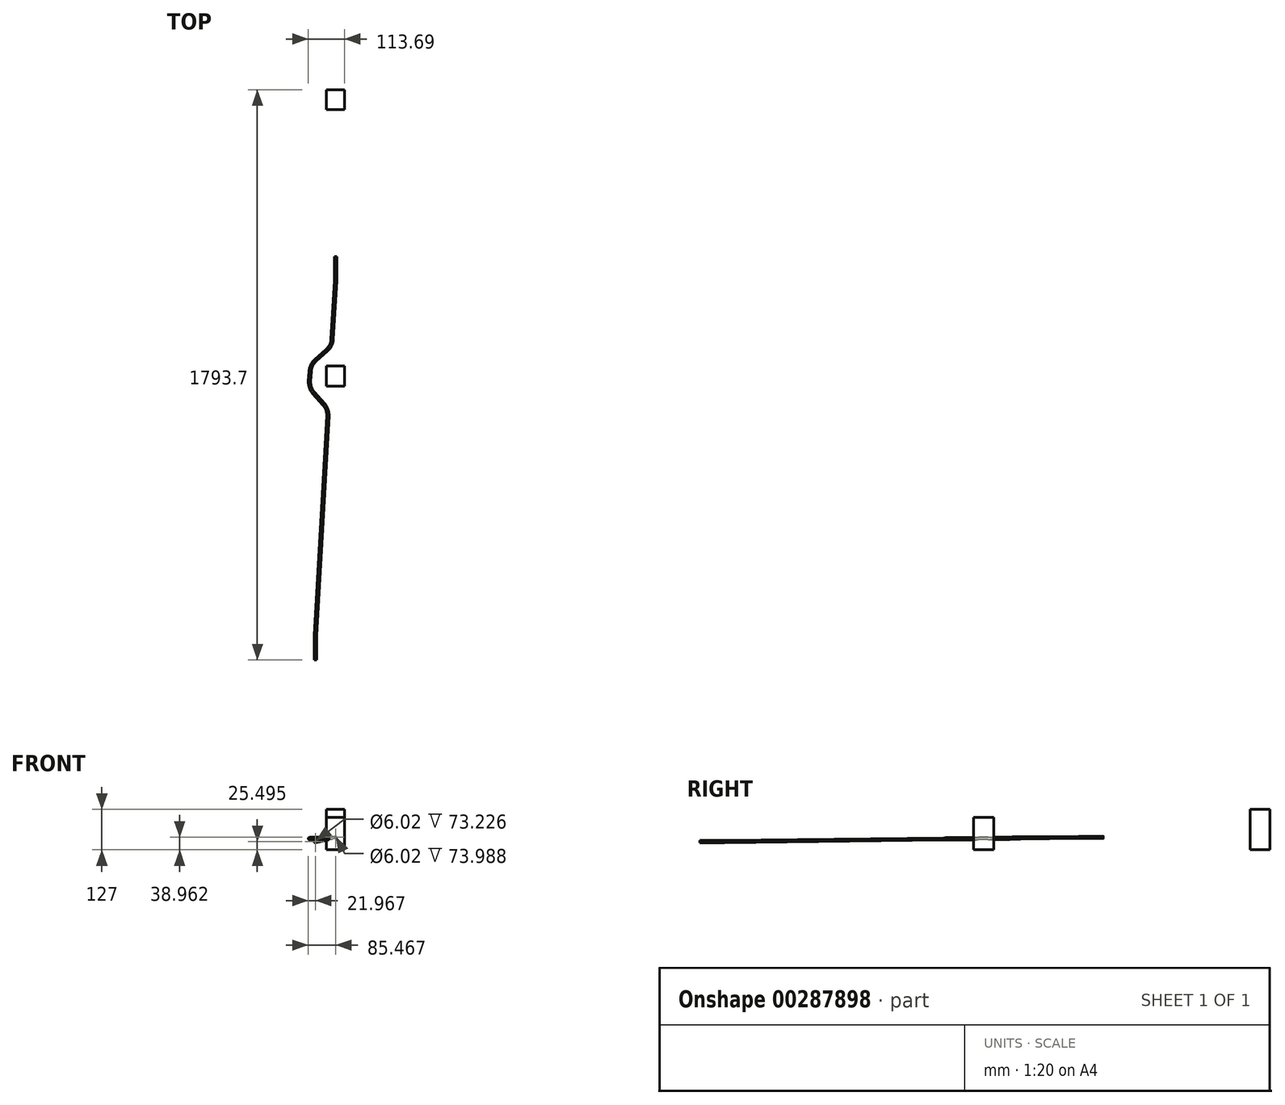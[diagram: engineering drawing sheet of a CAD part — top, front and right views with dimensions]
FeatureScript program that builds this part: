
annotation { "Feature Type Name" : "Feature", "Feature Type Description" : "" }
export const myFeature = defineFeature(function(context is Context, id is Id, definition is map)
    precondition{}
    {
        {
            var Q0;
            Q0=qCreatedBy(makeId("Top.planeOp"),FACE);
            var sketch = newSketch(context, id + "F0", { "sketchPlane" : qUnion([Q0])});
            skLineSegment(sketch, "E0", {"start": v(0, 0) * mm, "end": v(0.27, 0) * mm});
            skLineSegment(sketch, "E1", {"start": v(0.27, 0) * mm, "end": v(0.27, -58.44) * mm});
            skLineSegment(sketch, "E2", {"start": v(0.27, -58.44) * mm, "end": v(25.67, -58.44) * mm});
            skLineSegment(sketch, "E3", {"start": v(0, 0) * mm, "end": v(-63.23, 0) * mm});
            skLineSegment(sketch, "E4", {"start": v(-63.23, 0) * mm, "end": v(-63.23, -1327.88) * mm});
            skLineSegment(sketch, "E5", {"start": v(-63.23, -1327.88) * mm, "end": v(-37.83, -1327.88) * mm});
            skSolve(sketch);
        }
        {
            var Q0;
            Q0=sQuery(id+"F0.wireOp",EDGE,"E5");
            cPlane(context, id + "F1", {"entities" : qUnion([Q0]), "cplaneType" : CPlaneType.LINE_ANGLE, "offset" : 25.4 * mm, "angle" : 0 * degree, "width" : 152.4 * mm, "height" : 152.4 * mm});
        }
        {
            var Q0;
            Q0=sQuery(id+"F0.wireOp",EDGE,"E2");
            cPlane(context, id + "F2", {"entities" : qUnion([Q0]), "cplaneType" : CPlaneType.LINE_ANGLE, "offset" : 25.4 * mm, "angle" : 0 * degree, "width" : 152.4 * mm, "height" : 152.4 * mm});
        }
        {
            var Q0;
            Q0=qCreatedBy(id+"F2.planeOp",FACE);
            var sketch = newSketch(context, id + "F3", { "sketchPlane" : qUnion([Q0])});
            skLineSegment(sketch, "E6", {"start": v(-0.27, 0) * mm, "end": v(-0.27, 811.2) * mm});
            skSolve(sketch);
        }
        {
            var Q0;
            Q0=qCreatedBy(id+"F1.planeOp",FACE);
            var sketch = newSketch(context, id + "F4", { "sketchPlane" : qUnion([Q0])});
            skLineSegment(sketch, "E7", {"start": v(63.23, 0) * mm, "end": v(63.23, 797.74) * mm});
            skSolve(sketch);
        }
        {
            var Q0;
            Q0=sQuery(id+"F3.wireOp",EDGE,"E6");
            cPlane(context, id + "F5", {"entities" : qUnion([Q0]), "cplaneType" : CPlaneType.LINE_ANGLE, "offset" : 25.4 * mm, "angle" : 90 * degree, "width" : 152.4 * mm, "height" : 152.4 * mm});
        }
        {
            var Q0;
            Q0=sQuery(id+"F4.wireOp",EDGE,"E7");
            cPlane(context, id + "F6", {"entities" : qUnion([Q0]), "cplaneType" : CPlaneType.LINE_ANGLE, "offset" : 25.4 * mm, "angle" : 90 * degree, "width" : 152.4 * mm, "height" : 152.4 * mm});
        }
        {
            var Q0;
            Q0=qCreatedBy(id+"F5.planeOp",FACE);
            var sketch = newSketch(context, id + "F7", { "sketchPlane" : qUnion([Q0])});
            skCircle(sketch, "E8", {"center": v(-0.27, 811.2) * mm, "radius": 3.77 * mm});
            skSolve(sketch);
        }
        {
            var Q0;
            Q0=qCreatedBy(id+"F6.planeOp",FACE);
            var sketch = newSketch(context, id + "F8", { "sketchPlane" : qUnion([Q0])});
            skCircle(sketch, "E9", {"center": v(63.23, 797.74) * mm, "radius": 3.77 * mm});
            skSolve(sketch);
        }
        {
            var Q0;
            Q0=sQuery(id+"F3.wireOp",EDGE,"E6");
            cPlane(context, id + "F9", {"entities" : qUnion([Q0]), "cplaneType" : CPlaneType.LINE_ANGLE, "offset" : 25.4 * mm, "angle" : 0 * degree, "width" : 152.4 * mm, "height" : 152.4 * mm});
        }
        {
            var Q0;
            Q0=sQuery(id+"F4.wireOp",EDGE,"E7");
            cPlane(context, id + "F10", {"entities" : qUnion([Q0]), "cplaneType" : CPlaneType.LINE_ANGLE, "offset" : 25.4 * mm, "angle" : 0 * degree, "width" : 152.4 * mm, "height" : 152.4 * mm});
        }
        {
            var Q0;
            Q0=qCreatedBy(id+"F9.planeOp",FACE);
            var sketch = newSketch(context, id + "F11", { "sketchPlane" : qUnion([Q0])});
            skLineSegment(sketch, "E10", {"start": v(-58.44, 811.2) * mm, "end": v(-134.64, 811.2) * mm});
            skSolve(sketch);
        }
        {
            var Q0;
            Q0=qCreatedBy(id+"F10.planeOp",FACE);
            var sketch = newSketch(context, id + "F12", { "sketchPlane" : qUnion([Q0])});
            skLineSegment(sketch, "E11", {"start": v(-1327.88, 797.74) * mm, "end": v(-1251.68, 797.74) * mm});
            skSolve(sketch);
        }
        {
            var Q0;
            Q0=sQuery(id+"F11.wireOp",VERTEX,"E10.end");
            var Q1;
            Q1=sQuery(id+"F12.wireOp",VERTEX,"E11.end");
            var Q2;
            Q2=sQuery(id+"F11.wireOp",VERTEX,"E10.start");
            cPlane(context, id + "F13", {"entities" : qUnion([Q0, Q1, Q2]), "cplaneType" : CPlaneType.THREE_POINT, "offset" : 25.4 * mm, "width" : 152.4 * mm, "height" : 152.4 * mm});
        }
        {
            var Q0;
            Q0=qCreatedBy(id+"F13.planeOp",FACE);
            var sketch = newSketch(context, id + "F14", { "sketchPlane" : qUnion([Q0])});
            skLineSegment(sketch, "E12", {"start": v(168.43, -136.85) * mm, "end": v(103.65, -1251.68) * mm});
            skLineSegment(sketch, "E13", {"start": v(168.56, -132.43) * mm, "end": v(168.56, -58.44) * mm});
            skPoint(sketch, "E14.visualSharp", {"position": v(168.56, -134.64) * mm});
            skArc(sketch, "E14.filletArc", {"start": v(168.43, -136.85) * mm, "mid": v(168.53, -134.64) * mm, "end": v(168.56, -132.43) * mm});
            skSolve(sketch);
        }
        {
            var Q0;
            Q0=sQuery(id+"F14.wireOp",EDGE,"E12");
            var Q1;
            Q1=sQuery(id+"F12.wireOp",EDGE,"E11");
            cPlane(context, id + "F15", {"entities" : qUnion([Q0, Q1]), "cplaneType" : CPlaneType.LINE_ANGLE, "offset" : 25.4 * mm, "angle" : 0 * degree, "width" : 152.4 * mm, "height" : 152.4 * mm});
        }
        {
            var Q0;
            Q0=qCreatedBy(id+"F15.planeOp",FACE);
            var sketch = newSketch(context, id + "F16", { "sketchPlane" : qUnion([Q0])});
            skLineSegment(sketch, "E15", {"start": v(103.65, 1327.88) * mm, "end": v(103.65, 1253.9) * mm});
            skLineSegment(sketch, "E16", {"start": v(103.77, 1249.47) * mm, "end": v(168.43, 136.85) * mm});
            skPoint(sketch, "E17.visualSharp", {"position": v(103.65, 1251.68) * mm});
            skArc(sketch, "E17.filletArc", {"start": v(103.65, 1253.9) * mm, "mid": v(103.68, 1251.68) * mm, "end": v(103.77, 1249.47) * mm});
            skSolve(sketch);
        }
        {
            var Q0;
            Q0=makeQuery(id+"F8.imprint","IMPRINT",FACE,{"disambiguationData":[TD([[makeQuery(id+"F8.imprint","IMPRINT",EDGE,{"derivedFrom":sQuery(id+"F8.wireOp",EDGE,"E9")}),1.0]])]});
            var Q1;
            Q1=sQuery(id+"F16.wireOp",EDGE,"E15");
            var Q2;
            Q2=sQuery(id+"F16.wireOp",EDGE,"E17.filletArc");
            var Q3;
            Q3=sQuery(id+"F16.wireOp",EDGE,"E16");
            var Q4;
            Q4=sQuery(id+"F14.wireOp",EDGE,"E14.filletArc");
            var Q5;
            Q5=sQuery(id+"F14.wireOp",EDGE,"E13");
            sweep(context, id + "F17", {"profiles" : qUnion([Q0]), "path" : qUnion([Q1, Q2, Q3, Q4, Q5])});
        }
        {
            var Q0;
            Q0=makeQuery(id+"F17.opSweep","CAP_FACE",FACE,{"disambiguationData":[OSD([sQuery(id+"F8.wireOp",EDGE,"E9"),sQuery(id+"F16.wireOp",VERTEX,"E15.start")])],"isStart":true});
            shell(context, id + "F18", {"entities" : qUnion([Q0]), "thickness" : 0.76 * mm});
        }
        {
            var Q0;
            Q0=qCreatedBy(makeId("Top.planeOp"),FACE);
            var sketch = newSketch(context, id + "F19", { "sketchPlane" : qUnion([Q0])});
            skLineSegment(sketch, "E18", {"start": v(0, 0) * mm, "end": v(28.44, 0) * mm});
            skLineSegment(sketch, "E19", {"start": v(28.44, 0) * mm, "end": v(28.44, 465.82) * mm});
            skLineSegment(sketch, "E20", {"start": v(28.44, 465.82) * mm, "end": v(3.04, 465.82) * mm});
            skLineSegment(sketch, "E21", {"start": v(0, 0) * mm, "end": v(-27.96, 0) * mm});
            skLineSegment(sketch, "E22", {"start": v(-27.96, 0) * mm, "end": v(-27.96, 403.08) * mm});
            skLineSegment(sketch, "E23", {"start": v(-27.96, 403.08) * mm, "end": v(-53.36, 403.08) * mm});
            skSolve(sketch);
        }
        {
            var Q0;
            Q0=sQuery(id+"F19.wireOp",EDGE,"E20");
            cPlane(context, id + "F20", {"entities" : qUnion([Q0]), "cplaneType" : CPlaneType.LINE_ANGLE, "offset" : 25.4 * mm, "angle" : 0 * degree, "width" : 152.4 * mm, "height" : 152.4 * mm});
        }
        {
            var Q0;
            Q0=sQuery(id+"F19.wireOp",EDGE,"E23");
            cPlane(context, id + "F21", {"entities" : qUnion([Q0]), "cplaneType" : CPlaneType.LINE_ANGLE, "offset" : 25.4 * mm, "angle" : 0 * degree, "width" : 152.4 * mm, "height" : 152.4 * mm});
        }
        {
            var Q0;
            Q0=qCreatedBy(id+"F20.planeOp",FACE);
            var sketch = newSketch(context, id + "F22", { "sketchPlane" : qUnion([Q0])});
            skLineSegment(sketch, "E24", {"start": v(28.44, 0) * mm, "end": v(28.44, 772.24) * mm});
            skSolve(sketch);
        }
        {
            var Q0;
            Q0=qCreatedBy(id+"F21.planeOp",FACE);
            var sketch = newSketch(context, id + "F23", { "sketchPlane" : qUnion([Q0])});
            skLineSegment(sketch, "E25", {"start": v(-27.96, 0) * mm, "end": v(-27.96, 772.24) * mm});
            skLineSegment(sketch, "E26", {"start": v(-27.96, 772.24) * mm, "end": v(-53.36, 772.24) * mm});
            skSolve(sketch);
        }
        {
            var Q0;
            Q0=sQuery(id+"F23.wireOp",EDGE,"E26");
            cPlane(context, id + "F24", {"entities" : qUnion([Q0]), "cplaneType" : CPlaneType.LINE_ANGLE, "offset" : 25.4 * mm, "angle" : 90 * degree, "width" : 152.4 * mm, "height" : 152.4 * mm});
        }
        {
            var Q0;
            Q0=qCreatedBy(id+"F24.planeOp",FACE);
            var sketch = newSketch(context, id + "F25", { "sketchPlane" : qUnion([Q0])});
            skLineSegment(sketch, "E27.bottom", {"start": v(-27.96, 403.08) * mm, "end": v(28.44, 403.08) * mm});
            skLineSegment(sketch, "E27.top", {"start": v(-27.96, 465.82) * mm, "end": v(28.44, 465.82) * mm});
            skLineSegment(sketch, "E27.left", {"start": v(-27.96, 403.08) * mm, "end": v(-27.96, 465.82) * mm});
            skLineSegment(sketch, "E27.right", {"start": v(28.44, 403.08) * mm, "end": v(28.44, 465.82) * mm});
            skSolve(sketch);
        }
        {
            var Q0;
            Q0=qSketchRegion(id+"F25",true);
            extrude(context, id + "F26", {"entities" : qUnion([Q0]), "depth" : 127 * mm});
        }
        {
            var Q0;
            Q0=qCreatedBy(makeId("Top.planeOp"),FACE);
            var sketch = newSketch(context, id + "F27", { "sketchPlane" : qUnion([Q0])});
            skLineSegment(sketch, "E28", {"start": v(0, 0) * mm, "end": v(28.49, 0) * mm});
            skLineSegment(sketch, "E29", {"start": v(28.49, 0) * mm, "end": v(28.49, -403.6) * mm});
            skLineSegment(sketch, "E30", {"start": v(28.49, -403.6) * mm, "end": v(3.09, -403.6) * mm});
            skLineSegment(sketch, "E31", {"start": v(0, 0) * mm, "end": v(-27.9, 0) * mm});
            skLineSegment(sketch, "E32", {"start": v(-27.9, 0) * mm, "end": v(-27.9, -466.33) * mm});
            skLineSegment(sketch, "E33", {"start": v(-27.9, -466.33) * mm, "end": v(-53.3, -466.33) * mm});
            skSolve(sketch);
        }
        {
            var Q0;
            Q0=sQuery(id+"F27.wireOp",EDGE,"E33");
            cPlane(context, id + "F28", {"entities" : qUnion([Q0]), "cplaneType" : CPlaneType.LINE_ANGLE, "offset" : 25.4 * mm, "angle" : 0 * degree, "width" : 152.4 * mm, "height" : 152.4 * mm});
        }
        {
            var Q0;
            Q0=sQuery(id+"F27.wireOp",EDGE,"E30");
            cPlane(context, id + "F29", {"entities" : qUnion([Q0]), "cplaneType" : CPlaneType.LINE_ANGLE, "offset" : 25.4 * mm, "angle" : 0 * degree, "width" : 152.4 * mm, "height" : 152.4 * mm});
        }
        {
            var Q0;
            Q0=qCreatedBy(id+"F28.planeOp",FACE);
            var sketch = newSketch(context, id + "F30", { "sketchPlane" : qUnion([Q0])});
            skLineSegment(sketch, "E34", {"start": v(-27.9, 0) * mm, "end": v(-27.9, 772.24) * mm});
            skLineSegment(sketch, "E35", {"start": v(-27.9, 772.24) * mm, "end": v(-2.5, 772.24) * mm});
            skSolve(sketch);
        }
        {
            var Q0;
            Q0=qCreatedBy(id+"F29.planeOp",FACE);
            var sketch = newSketch(context, id + "F31", { "sketchPlane" : qUnion([Q0])});
            skLineSegment(sketch, "E36", {"start": v(28.49, 0) * mm, "end": v(28.49, 772.24) * mm});
            skSolve(sketch);
        }
        {
            var Q0;
            Q0=sQuery(id+"F30.wireOp",EDGE,"E35");
            cPlane(context, id + "F32", {"entities" : qUnion([Q0]), "cplaneType" : CPlaneType.LINE_ANGLE, "offset" : 25.4 * mm, "angle" : 90 * degree, "width" : 152.4 * mm, "height" : 152.4 * mm});
        }
        {
            var Q0;
            Q0=qCreatedBy(id+"F32.planeOp",FACE);
            var sketch = newSketch(context, id + "F33", { "sketchPlane" : qUnion([Q0])});
            skLineSegment(sketch, "E37.bottom", {"start": v(-27.9, -466.33) * mm, "end": v(28.49, -466.33) * mm});
            skLineSegment(sketch, "E37.top", {"start": v(-27.9, -403.6) * mm, "end": v(28.49, -403.6) * mm});
            skLineSegment(sketch, "E37.left", {"start": v(-27.9, -466.33) * mm, "end": v(-27.9, -403.6) * mm});
            skLineSegment(sketch, "E37.right", {"start": v(28.49, -466.33) * mm, "end": v(28.49, -403.6) * mm});
            skSolve(sketch);
        }
        {
            var Q0;
            Q0=qSketchRegion(id+"F33",true);
            extrude(context, id + "F34", {"entities" : qUnion([Q0]), "depth" : 101.6 * mm});
        }
        {
            var Q0;
            Q0=makeQuery(id+"F17.opSweep","SWEPT_BODY",BODY,{"disambiguationData":[OSD([sQuery(id+"F8.wireOp",EDGE,"E9"),sQuery(id+"F14.wireOp",EDGE,"E13")])]});
            deleteBodies(context, id + "F35", {"entities" : qUnion([Q0])});
        }
        {
            var Q0;
            Q0=sQuery(id+"F16.wireOp",EDGE,"E16");
            cPlane(context, id + "F36", {"entities" : qUnion([Q0]), "cplaneType" : CPlaneType.LINE_ANGLE, "offset" : 25.4 * mm, "angle" : 0 * degree, "width" : 152.4 * mm, "height" : 152.4 * mm});
        }
        {
            var Q0;
            Q0=qCreatedBy(id+"F36.planeOp",FACE);
            var sketch = newSketch(context, id + "F37", { "sketchPlane" : qUnion([Q0])});
            skLineSegment(sketch, "E38", {"start": v(-22.75, -529.71) * mm, "end": v(-11.4, -329.93) * mm});
            skLineSegment(sketch, "E39", {"start": v(-27.1, -343.94) * mm, "end": v(-62.7, -375.72) * mm});
            skLineSegment(sketch, "E40", {"start": v(-79.59, -410.73) * mm, "end": v(-81.35, -441.7) * mm});
            skLineSegment(sketch, "E41", {"start": v(-68.53, -478.4) * mm, "end": v(-36.76, -514.01) * mm});
            skLineSegment(sketch, "E42", {"start": v(-82.54, -462.7) * mm, "end": v(-19.14, -466.31) * mm});
            skPoint(sketch, "E43.visualSharp", {"position": v(-78.4, -389.73) * mm});
            skArc(sketch, "E43.filletArc", {"start": v(-62.7, -375.72) * mm, "mid": v(-74.62, -391.55) * mm, "end": v(-79.59, -410.73) * mm});
            skPoint(sketch, "E44.visualSharp", {"position": v(-82.54, -462.7) * mm});
            skArc(sketch, "E44.filletArc", {"start": v(-81.35, -441.7) * mm, "mid": v(-78.59, -461.33) * mm, "end": v(-68.53, -478.4) * mm});
            skLineSegment(sketch, "E45", {"start": v(-23.94, -550.72) * mm, "end": v(-63.1, -1239.77) * mm});
            skLineSegment(sketch, "E46", {"start": v(-10.2, -308.92) * mm, "end": v(0.14, -127.06) * mm});
            skPoint(sketch, "E47.visualSharp", {"position": v(-22.75, -529.71) * mm});
            skArc(sketch, "E47.filletArc", {"start": v(-23.94, -550.72) * mm, "mid": v(-26.7, -531.1) * mm, "end": v(-36.76, -514.01) * mm});
            skPoint(sketch, "E48.visualSharp", {"position": v(-11.4, -329.93) * mm});
            skArc(sketch, "E48.filletArc", {"start": v(-27.1, -343.94) * mm, "mid": v(-15.16, -328.11) * mm, "end": v(-10.2, -308.92) * mm});
            skSolve(sketch);
        }
        {
            var Q0;
            Q0=makeQuery(id+"F7.imprint","IMPRINT",FACE,{"disambiguationData":[TD([[makeQuery(id+"F7.imprint","IMPRINT",EDGE,{"derivedFrom":sQuery(id+"F7.wireOp",EDGE,"E8")}),1.0]])]});
            var Q1;
            Q1=sQuery(id+"F14.wireOp",EDGE,"E13");
            var Q2;
            Q2=sQuery(id+"F14.wireOp",EDGE,"E14.filletArc");
            var Q3;
            Q3=sQuery(id+"F37.wireOp",EDGE,"E46");
            var Q4;
            Q4=sQuery(id+"F37.wireOp",EDGE,"E48.filletArc");
            var Q5;
            Q5=sQuery(id+"F37.wireOp",EDGE,"E39");
            var Q6;
            Q6=sQuery(id+"F37.wireOp",EDGE,"E43.filletArc");
            var Q7;
            Q7=sQuery(id+"F37.wireOp",EDGE,"E40");
            var Q8;
            Q8=sQuery(id+"F37.wireOp",EDGE,"E44.filletArc");
            var Q9;
            Q9=sQuery(id+"F37.wireOp",EDGE,"E41");
            var Q10;
            Q10=sQuery(id+"F37.wireOp",EDGE,"E47.filletArc");
            var Q11;
            Q11=sQuery(id+"F37.wireOp",EDGE,"E45");
            var Q12;
            Q12=sQuery(id+"F16.wireOp",EDGE,"E17.filletArc");
            var Q13;
            Q13=sQuery(id+"F16.wireOp",EDGE,"E15");
            sweep(context, id + "F38", {"profiles" : qUnion([Q0]), "path" : qUnion([Q1, Q2, Q3, Q4, Q5, Q6, Q7, Q8, Q9, Q10, Q11, Q12, Q13])});
        }
        {
            var Q0;
            Q0=makeQuery(id+"F38.opSweep","CAP_FACE",FACE,{"disambiguationData":[OSD([sQuery(id+"F7.wireOp",EDGE,"E8"),sQuery(id+"F14.wireOp",VERTEX,"E13.end")])],"isStart":true});
            shell(context, id + "F39", {"entities" : qUnion([Q0]), "thickness" : 0.76 * mm});
        }
    });
